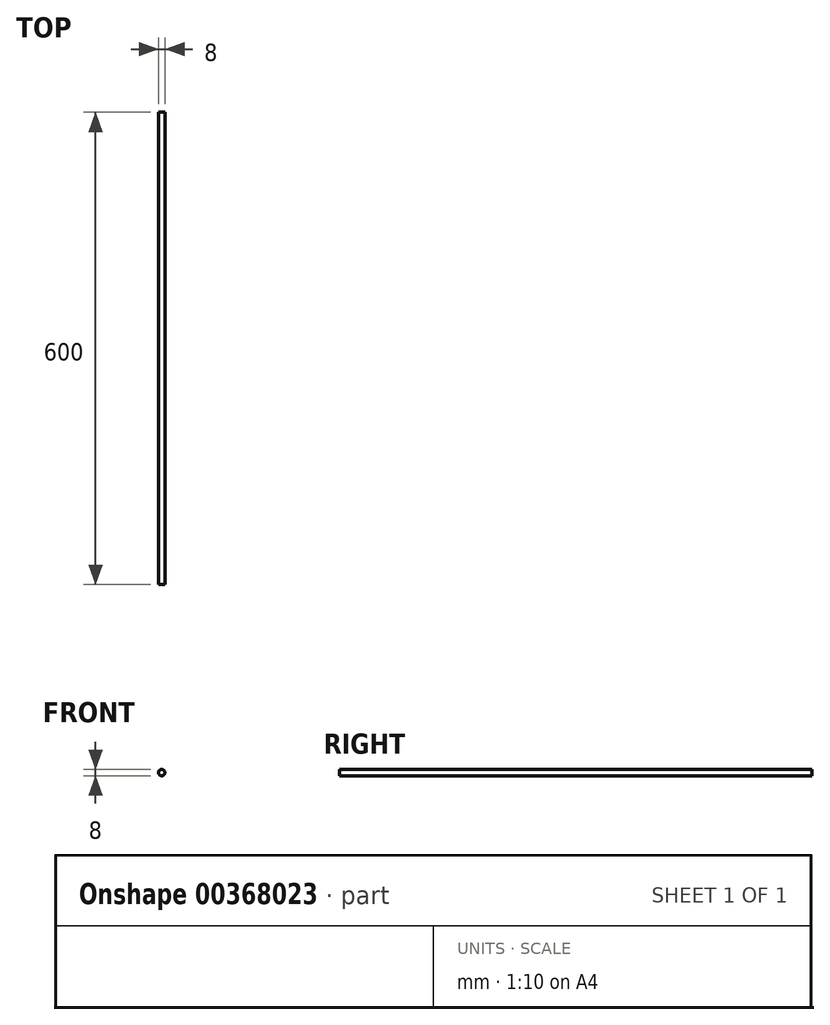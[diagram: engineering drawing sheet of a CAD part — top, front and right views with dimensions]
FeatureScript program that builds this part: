
annotation { "Feature Type Name" : "Feature", "Feature Type Description" : "" }
export const myFeature = defineFeature(function(context is Context, id is Id, definition is map)
    precondition{}
    {
        {
            var Q0;
            Q0=qCreatedBy(makeId("Front.planeOp"),FACE);
            var sketch = newSketch(context, id + "F0", { "sketchPlane" : qUnion([Q0])});
            skCircle(sketch, "E0", {"center": v(0, 0) * mm, "radius": 4 * mm});
            skSolve(sketch);
        }
        {
            var Q0;
            Q0=makeQuery(id+"F0.imprint","IMPRINT",FACE,{"disambiguationData":[TD([[makeQuery(id+"F0.imprint","IMPRINT",EDGE,{"derivedFrom":sQuery(id+"F0.wireOp",EDGE,"E0")}),1.0]])]});
            extrude(context, id + "F1", {"entities" : qUnion([Q0]), "depth" : 600 * mm});
        }
    });
